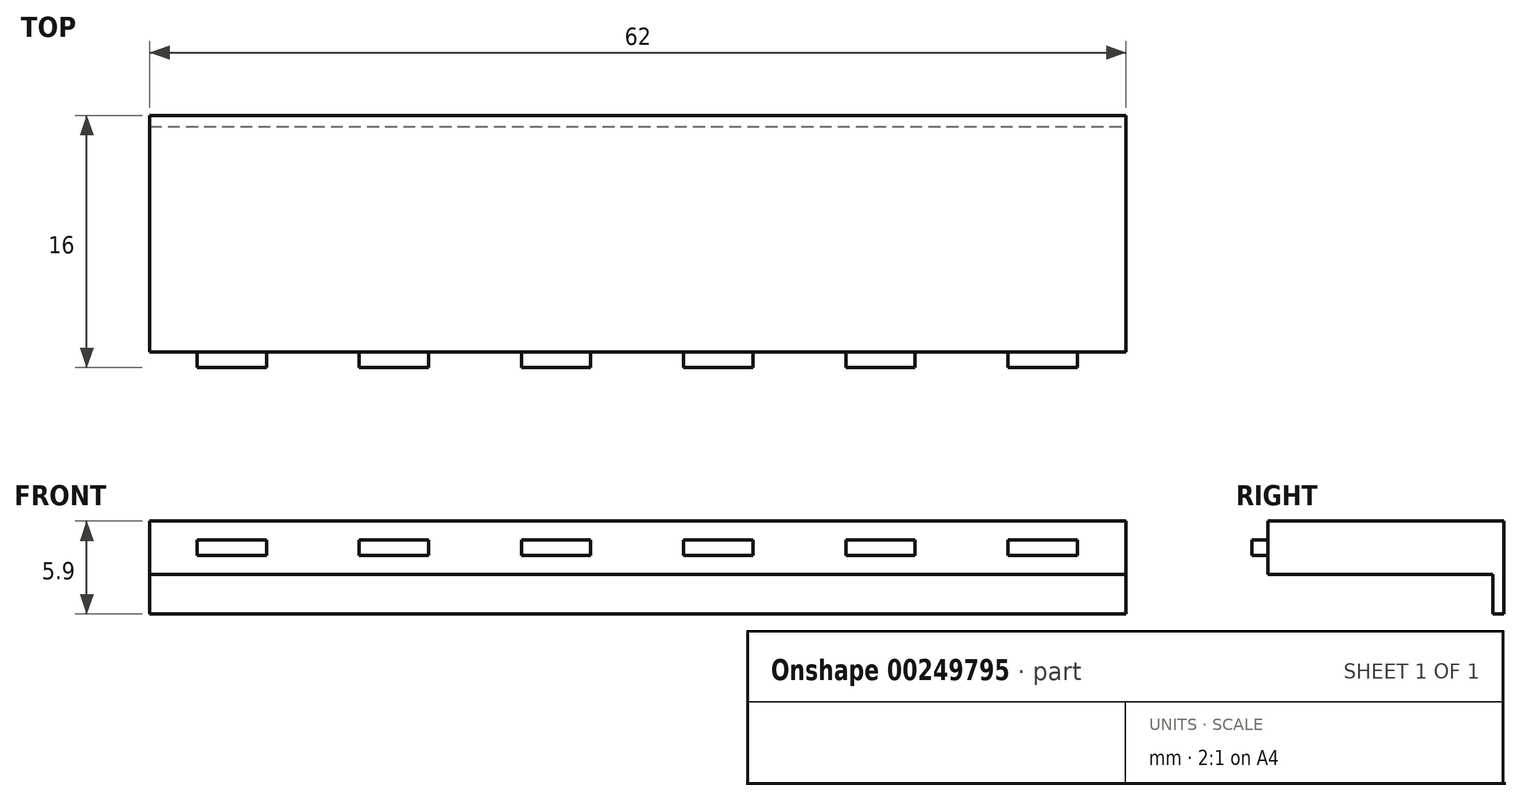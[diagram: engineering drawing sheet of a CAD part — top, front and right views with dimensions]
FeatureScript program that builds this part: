
annotation { "Feature Type Name" : "Feature", "Feature Type Description" : "" }
export const myFeature = defineFeature(function(context is Context, id is Id, definition is map)
    precondition{}
    {
        {
            var Q0;
            Q0=qCreatedBy(makeId("Top.planeOp"),FACE);
            var sketch = newSketch(context, id + "F0", { "sketchPlane" : qUnion([Q0])});
            skLineSegment(sketch, "E0.bottom", {"start": v(31, -7.5) * mm, "end": v(-31, -7.5) * mm});
            skLineSegment(sketch, "E0.top", {"start": v(31, 7.5) * mm, "end": v(-31, 7.5) * mm});
            skLineSegment(sketch, "E0.left", {"start": v(31, -7.5) * mm, "end": v(31, 7.5) * mm});
            skLineSegment(sketch, "E0.right", {"start": v(-31, -7.5) * mm, "end": v(-31, 7.5) * mm});
            skPoint(sketch, "E0.middle", {"position": v(0, 0) * mm});
            skSolve(sketch);
        }
        {
            var Q0;
            Q0=makeQuery(id+"F0.imprint","IMPRINT",FACE,{"disambiguationData":[TD([[makeQuery(id+"F0.imprint","IMPRINT",EDGE,{"derivedFrom":sQuery(id+"F0.wireOp",EDGE,"E0.bottom")}),-1.0]])]});
            extrude(context, id + "F1", {"entities" : qUnion([Q0]), "depth" : 3.4 * mm});
        }
        {
            var Q0;
            Q0=makeQuery(id+"F1.opExtrude","CAP_FACE",FACE,{"disambiguationData":[OSD([sQuery(id+"F0.wireOp",EDGE,"E0.bottom"),sQuery(id+"F0.wireOp",EDGE,"E0.top"),sQuery(id+"F0.wireOp",EDGE,"E0.left"),sQuery(id+"F0.wireOp",EDGE,"E0.right")])],"isStart":true});
            var sketch = newSketch(context, id + "F2", { "sketchPlane" : qUnion([Q0])});
            skLineSegment(sketch, "E1.0.0", {"start": v(31, -7.5) * mm, "end": v(31, 7.5) * mm});
            skLineSegment(sketch, "E1.0.1", {"start": v(31, 7.5) * mm, "end": v(-31, 7.5) * mm});
            skLineSegment(sketch, "E1.0.2", {"start": v(-31, 7.5) * mm, "end": v(-31, -7.5) * mm});
            skLineSegment(sketch, "E1.0.3", {"start": v(-31, -7.5) * mm, "end": v(31, -7.5) * mm});
            skLineSegment(sketch, "E2.top", {"start": v(-31, -6.8) * mm, "end": v(31, -6.8) * mm});
            skLineSegment(sketch, "E2.left", {"start": v(-31, -7.5) * mm, "end": v(-31, -6.8) * mm});
            skLineSegment(sketch, "E2.right", {"start": v(31, -7.5) * mm, "end": v(31, -6.8) * mm});
            skSolve(sketch);
        }
        {
            var Q0;
            Q0=makeQuery(id+"F2.imprint","IMPRINT",FACE,{"disambiguationData":[TD([[makeQuery(id+"F2.imprint","IMPRINT",EDGE,{"derivedFrom":sQuery(id+"F2.wireOp",EDGE,"E1.0.3")}),-1.0]])]});
            extrude(context, id + "F3", {"entities" : qUnion([Q0]), "operationType" : NewBodyOperationType.ADD, "depth" : 2.5 * mm});
        }
        {
            var Q0;
            Q0=makeQuery(id+"F1.opExtrude","SWEPT_FACE",FACE,{"disambiguationData":[OSD([sQuery(id+"F0.wireOp",EDGE,"E0.bottom")])]});
            var sketch = newSketch(context, id + "F4", { "sketchPlane" : qUnion([Q0])});
            skLineSegment(sketch, "E3", {"start": v(-31, 1.7) * mm, "end": v(31, 1.7) * mm, "construction": true});
            skLineSegment(sketch, "E4.bottom", {"start": v(-23.6, 1.2) * mm, "end": v(-28, 1.2) * mm});
            skLineSegment(sketch, "E4.top", {"start": v(-23.6, 2.2) * mm, "end": v(-28, 2.2) * mm});
            skLineSegment(sketch, "E4.left", {"start": v(-23.6, 1.2) * mm, "end": v(-23.6, 2.2) * mm});
            skLineSegment(sketch, "E4.right", {"start": v(-28, 1.2) * mm, "end": v(-28, 2.2) * mm});
            skPoint(sketch, "E4.middle", {"position": v(-25.8, 1.7) * mm});
            skLineSegment(sketch, "E5.1.0.0", {"start": v(-13.3, 1.2) * mm, "end": v(-13.3, 2.2) * mm});
            skLineSegment(sketch, "E5.1.0.1", {"start": v(-13.3, 2.2) * mm, "end": v(-17.7, 2.2) * mm});
            skLineSegment(sketch, "E5.1.0.2", {"start": v(-17.7, 1.2) * mm, "end": v(-17.7, 2.2) * mm});
            skLineSegment(sketch, "E5.1.0.3", {"start": v(-13.3, 1.2) * mm, "end": v(-17.7, 1.2) * mm});
            skLineSegment(sketch, "E5.2.0.0", {"start": v(-3, 1.2) * mm, "end": v(-3, 2.2) * mm});
            skLineSegment(sketch, "E5.2.0.1", {"start": v(-3, 2.2) * mm, "end": v(-7.4, 2.2) * mm});
            skLineSegment(sketch, "E5.2.0.2", {"start": v(-7.4, 1.2) * mm, "end": v(-7.4, 2.2) * mm});
            skLineSegment(sketch, "E5.2.0.3", {"start": v(-3, 1.2) * mm, "end": v(-7.4, 1.2) * mm});
            skLineSegment(sketch, "E5.3.0.0", {"start": v(7.3, 1.2) * mm, "end": v(7.3, 2.2) * mm});
            skLineSegment(sketch, "E5.3.0.1", {"start": v(7.3, 2.2) * mm, "end": v(2.9, 2.2) * mm});
            skLineSegment(sketch, "E5.3.0.2", {"start": v(2.9, 1.2) * mm, "end": v(2.9, 2.2) * mm});
            skLineSegment(sketch, "E5.3.0.3", {"start": v(7.3, 1.2) * mm, "end": v(2.9, 1.2) * mm});
            skLineSegment(sketch, "E5.4.0.0", {"start": v(17.6, 1.2) * mm, "end": v(17.6, 2.2) * mm});
            skLineSegment(sketch, "E5.4.0.1", {"start": v(17.6, 2.2) * mm, "end": v(13.2, 2.2) * mm});
            skLineSegment(sketch, "E5.4.0.2", {"start": v(13.2, 1.2) * mm, "end": v(13.2, 2.2) * mm});
            skLineSegment(sketch, "E5.4.0.3", {"start": v(17.6, 1.2) * mm, "end": v(13.2, 1.2) * mm});
            skLineSegment(sketch, "E5.5.0.0", {"start": v(27.9, 1.2) * mm, "end": v(27.9, 2.2) * mm});
            skLineSegment(sketch, "E5.5.0.1", {"start": v(27.9, 2.2) * mm, "end": v(23.5, 2.2) * mm});
            skLineSegment(sketch, "E5.5.0.2", {"start": v(23.5, 1.2) * mm, "end": v(23.5, 2.2) * mm});
            skLineSegment(sketch, "E5.5.0.3", {"start": v(27.9, 1.2) * mm, "end": v(23.5, 1.2) * mm});
            skLineSegment(sketch, "E5.direction1", {"start": v(-23.6, 1.2) * mm, "end": v(-13.3, 1.2) * mm, "construction": true});
            skSolve(sketch);
        }
        {
            var Q0;
            Q0=makeQuery(id+"F4.imprint","IMPRINT",FACE,{"disambiguationData":[TD([[makeQuery(id+"F4.imprint","IMPRINT",EDGE,{"derivedFrom":sQuery(id+"F4.wireOp",EDGE,"E4.bottom")}),-1.0]])]});
            var Q1;
            Q1=makeQuery(id+"F4.imprint","IMPRINT",FACE,{"disambiguationData":[TD([[makeQuery(id+"F4.imprint","IMPRINT",EDGE,{"derivedFrom":sQuery(id+"F4.wireOp",EDGE,"E5.1.0.0")}),1.0]])]});
            var Q2;
            Q2=makeQuery(id+"F4.imprint","IMPRINT",FACE,{"disambiguationData":[TD([[makeQuery(id+"F4.imprint","IMPRINT",EDGE,{"derivedFrom":sQuery(id+"F4.wireOp",EDGE,"E5.2.0.0")}),1.0]])]});
            var Q3;
            Q3=makeQuery(id+"F4.imprint","IMPRINT",FACE,{"disambiguationData":[TD([[makeQuery(id+"F4.imprint","IMPRINT",EDGE,{"derivedFrom":sQuery(id+"F4.wireOp",EDGE,"E5.3.0.0")}),1.0]])]});
            var Q4;
            Q4=makeQuery(id+"F4.imprint","IMPRINT",FACE,{"disambiguationData":[TD([[makeQuery(id+"F4.imprint","IMPRINT",EDGE,{"derivedFrom":sQuery(id+"F4.wireOp",EDGE,"E5.4.0.0")}),1.0]])]});
            var Q5;
            Q5=makeQuery(id+"F4.imprint","IMPRINT",FACE,{"disambiguationData":[TD([[makeQuery(id+"F4.imprint","IMPRINT",EDGE,{"derivedFrom":sQuery(id+"F4.wireOp",EDGE,"E5.5.0.0")}),1.0]])]});
            extrude(context, id + "F5", {"entities" : qUnion([Q0, Q1, Q2, Q3, Q4, Q5]), "operationType" : NewBodyOperationType.ADD, "depth" : 1 * mm});
        }
    });
